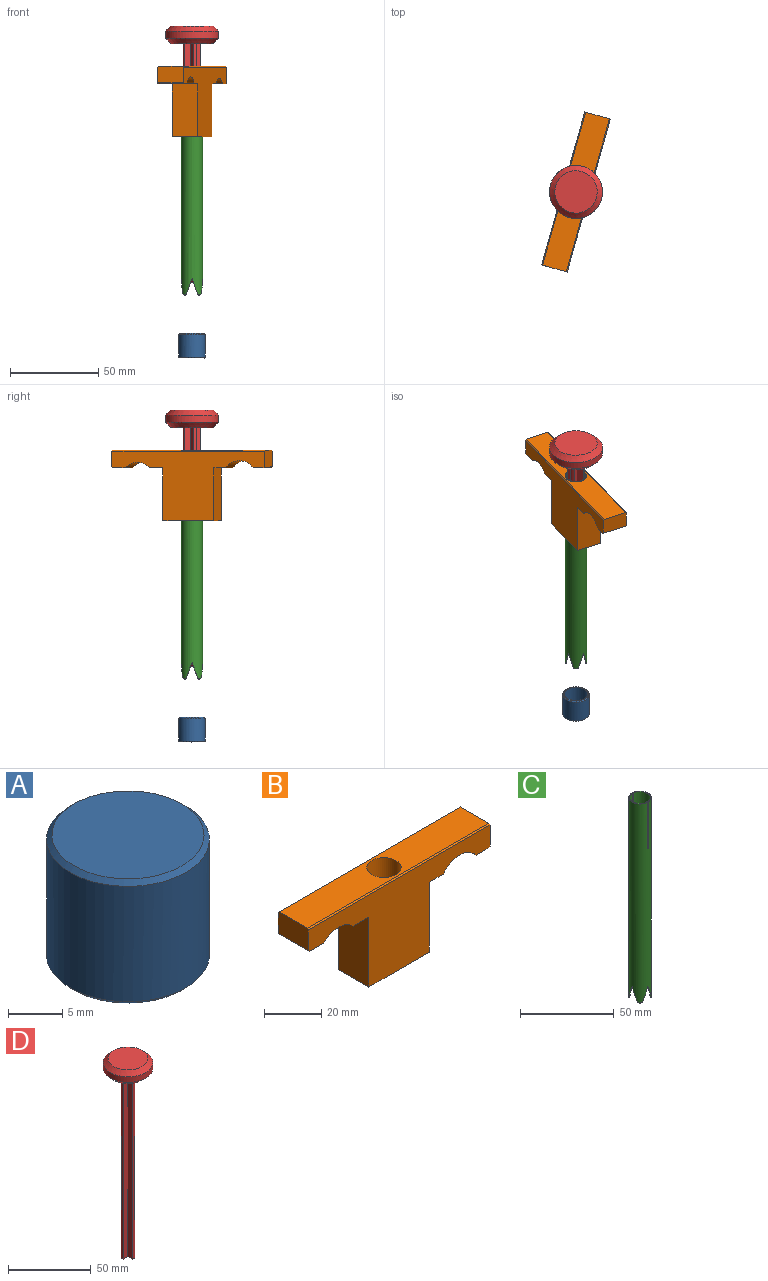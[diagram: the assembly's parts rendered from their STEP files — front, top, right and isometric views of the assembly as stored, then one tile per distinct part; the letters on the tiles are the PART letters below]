
ASSEMBLY  parts=4 mates=4
PART A: 7 faces, bbox 15x15x14 mm
  f0: cylinder r=6.5mm len=13mm, axis (0,0,-1), area 530.9mm2, adj f1,f4
  f1: plane 14x14mm, normal (0,0,-1), area 21.2mm2, adj f0,f5
  f2: cylinder r=7.5mm len=15mm, axis (0,0,-1), area 612.6mm2, adj f5,f6
  f3: plane 14x14mm, normal (0,0,1), area 153.9mm2, adj f6
  f4: plane 13x13mm, normal (0,0,-1), area 132.7mm2, adj f0
  f5: cone r=7mm half-angle=45deg, axis (0,0,1), area 32.2mm2, adj f1,f2
  f6: cone r=7.5mm half-angle=45deg, axis (0,0,-1), area 32.2mm2, adj f2,f3
PART B: 19 faces, bbox 90x15x40 mm
  f0: plane 15x6.91mm, normal (0,0,-1), area 103.6mm2, adj f3,f10,f11,f14
  f1: plane 15x7.73mm, normal (0,0,-1), area 116mm2, adj f9,f10,f11,f13
  f2: plane 30x15mm, normal (0,0,-1), area 336.9mm2, adj f3,f9,f10,f11,f12
  f3: plane 30x15mm, normal (1,0,0), area 450mm2, adj f0,f2,f10,f11
  f4: plane 15x6.41mm, normal (0,0,-1), area 96.1mm2, adj f10,f11,f14,f18
  f5: plane 15x9.5mm, normal (1,0,0), area 142.2mm2, adj f6,f10,f11,f15,f16,f18
  f6: plane 90x14mm, normal (0,0,1), area 1146.9mm2, adj f5,f7,f12,f15,f16
  f7: plane 15x9.5mm, normal (-1,0,0), area 142.2mm2, adj f6,f10,f11,f15,f16,f17
  f8: plane 15x7.23mm, normal (0,0,-1), area 108.5mm2, adj f10,f11,f13,f17
  f9: plane 30x15mm, normal (-1,0,0), area 450mm2, adj f1,f2,f10,f11
  f10: plane 90x39.5mm, normal (0,-1,0), area 1676.6mm2, adj f0,f1,f2,f3,f4,f5,f7,f8
  f11: plane 90x39.5mm, normal (0,1,0), area 1676.6mm2, adj f0,f1,f2,f3,f4,f5,f7,f8
  f12: cylinder r=6mm len=40mm, axis (0,0,-1), area 1508mm2, adj f2,f6
  f13: cylinder r=10mm len=15mm, axis (0,-1,0), area 244mm2, adj f1,f8,f10,f11
  f14: cylinder r=10mm len=16.19mm, axis (0,-1,0), area 282.9mm2, adj f0,f4,f10,f11
  f15: plane 90x0.5mm, normal (0,0.71,0.71), area 63.6mm2, adj f5,f6,f7,f11
  f16: plane 90x0.5mm, normal (0,-0.71,0.71), area 63.6mm2, adj f5,f6,f7,f10
  f17: plane 15x0.5mm, normal (-0.71,0,-0.71), area 10.6mm2, adj f7,f8,f10,f11
  f18: plane 15x0.5mm, normal (0.71,0,-0.71), area 10.6mm2, adj f4,f5,f10,f11
PART C: 22 faces, bbox 12x12x130 mm
  f0: plane 11.99x5.75mm, normal (0,0,1), area 8.8mm2, adj f1,f3,f12,f17
  f1: cylinder r=6mm len=129.5mm, axis (0,0,-1), area 4722.1mm2, adj f0,f2,f4,f5,f6,f7,f8,f9
  f2: plane 11.99x5.75mm, normal (0,0,1), area 8.8mm2, adj f1,f3,f14,f15
  f3: cylinder r=5.5mm len=130mm, axis (0,0,-1), area 4317mm2, adj f0,f2,f4,f5,f6,f7,f8,f9
  f4: plane 10x3.5mm, normal (0,0.94,-0.33), area 5.5mm2, adj f1,f3,f5,f20
  f5: plane 10x3.5mm, normal (0,-0.94,-0.33), area 5.5mm2, adj f1,f3,f4,f19
  f6: plane 10x3.5mm, normal (0,-0.94,-0.33), area 5.5mm2, adj f1,f3,f7,f21
  f7: plane 10x3.5mm, normal (0,0.94,-0.33), area 5.5mm2, adj f1,f3,f6,f18
  f8: plane 10x3.5mm, normal (0.94,0,-0.33), area 5.5mm2, adj f1,f3,f9,f18
  f9: plane 10x3.5mm, normal (-0.94,0,-0.33), area 5.5mm2, adj f1,f3,f8,f20
  f10: plane 10x3.5mm, normal (-0.94,0,-0.33), area 5.5mm2, adj f1,f3,f11,f19
  f11: plane 10x3.5mm, normal (0.94,0,-0.33), area 5.5mm2, adj f1,f3,f10,f21
  f12: plane 30x0.5mm, normal (-1,0,0), area 15mm2, adj f0,f1,f3,f13
  f13: plane 0.51x0.5mm, normal (0,0,1), area 0.3mm2, adj f1,f3,f12,f14
  f14: plane 30x0.5mm, normal (1,0,0), area 15mm2, adj f1,f2,f3,f13
  f15: plane 30x0.5mm, normal (1,0,0), area 15mm2, adj f1,f2,f3,f16
  f16: plane 0.51x0.5mm, normal (0,0,1), area 0.3mm2, adj f1,f3,f15,f17
  f17: plane 30x0.5mm, normal (-1,0,0), area 15mm2, adj f0,f1,f3,f16
  f18: cone r=6mm half-angle=45deg, axis (0,0,1), area 1.2mm2, adj f1,f3,f7,f8
  f19: cone r=6mm half-angle=45deg, axis (0,0,1), area 1.2mm2, adj f1,f3,f5,f10
  f20: cone r=6mm half-angle=45deg, axis (0,0,1), area 1.2mm2, adj f1,f3,f4,f9
  f21: cone r=6mm half-angle=45deg, axis (0,0,1), area 1.2mm2, adj f1,f3,f6,f11
PART D: 18 faces, bbox 30x30x145 mm
  f0: plane 10x10mm, normal (0,0,-1), area 35.7mm2, adj f4,f5,f6,f7,f8,f9,f10,f11
  f1: plane 24x24mm, normal (0,0,-1), area 416.7mm2, adj f4,f5,f6,f7,f8,f9,f10,f11
  f2: cylinder r=15mm len=30mm, axis (0,0,-1), area 377mm2, adj f12,f13
  f3: plane 24x24mm, normal (0,0,1), area 452.4mm2, adj f13
  f4: plane 135x3.9mm, normal (1,0,0), area 526.4mm2, adj f0,f1,f5,f16
  f5: plane 135x3.9mm, normal (0,1,0), area 526.4mm2, adj f0,f1,f4,f15
  f6: plane 135x3.9mm, normal (-1,0,0), area 526.4mm2, adj f0,f1,f7,f14
  f7: plane 135x3.9mm, normal (0,-1,0), area 526.4mm2, adj f0,f1,f6,f17
  f8: plane 135x3.9mm, normal (0,1,0), area 526.4mm2, adj f0,f1,f9,f17
  f9: plane 135x3.9mm, normal (-1,0,0), area 526.4mm2, adj f0,f1,f8,f16
  f10: plane 135x3.9mm, normal (0,-1,0), area 526.4mm2, adj f0,f1,f11,f15
  f11: plane 135x3.9mm, normal (1,0,0), area 526.4mm2, adj f0,f1,f10,f14
  f12: cone r=12mm half-angle=45deg, axis (0,0,1), area 359.9mm2, adj f1,f2
  f13: cone r=15mm half-angle=45deg, axis (0,0,-1), area 359.9mm2, adj f2,f3
  f14: cylinder r=5mm len=135mm, axis (0,0,-1), area 271.8mm2, adj f0,f1,f6,f11
  f15: cylinder r=5mm len=135mm, axis (0,0,-1), area 271.8mm2, adj f0,f1,f5,f10
  f16: cylinder r=5mm len=135mm, axis (0,0,-1), area 271.8mm2, adj f0,f1,f4,f9
  f17: cylinder r=5mm len=135mm, axis (0,0,-1), area 271.8mm2, adj f0,f1,f7,f8
PLACE A rot(axis=(1,0.06,0),180deg) t=(-115.02,-45.82,-322.32)mm
PLACE B rot(axis=(0,0,-1),105.7deg) t=(-115.02,-45.82,-211.07)mm
PLACE C rot(axis=(0,0,1),0deg) t=(-115.02,-45.82,-301.07)mm fixed
PLACE D rot(axis=(0,0,1),20.5deg) t=(-115.02,-45.82,-293.3)mm
MATE cylindrical D.f12 <-> C.f1  axis (0,0,1) through (-115.02,-45.82,-151.3)mm
MATE planar C.f0 <-> B.f12  axis (0,0,1) through (-111.26,-45.82,-171.07)mm
MATE cylindrical A.f0 <-> C.f1  axis (0,0,1) through (-115.02,-45.82,-329.32)mm
MATE cylindrical B.f12 <-> C.f1  axis (0,0,-1) through (-115.02,-45.82,-211.07)mm
